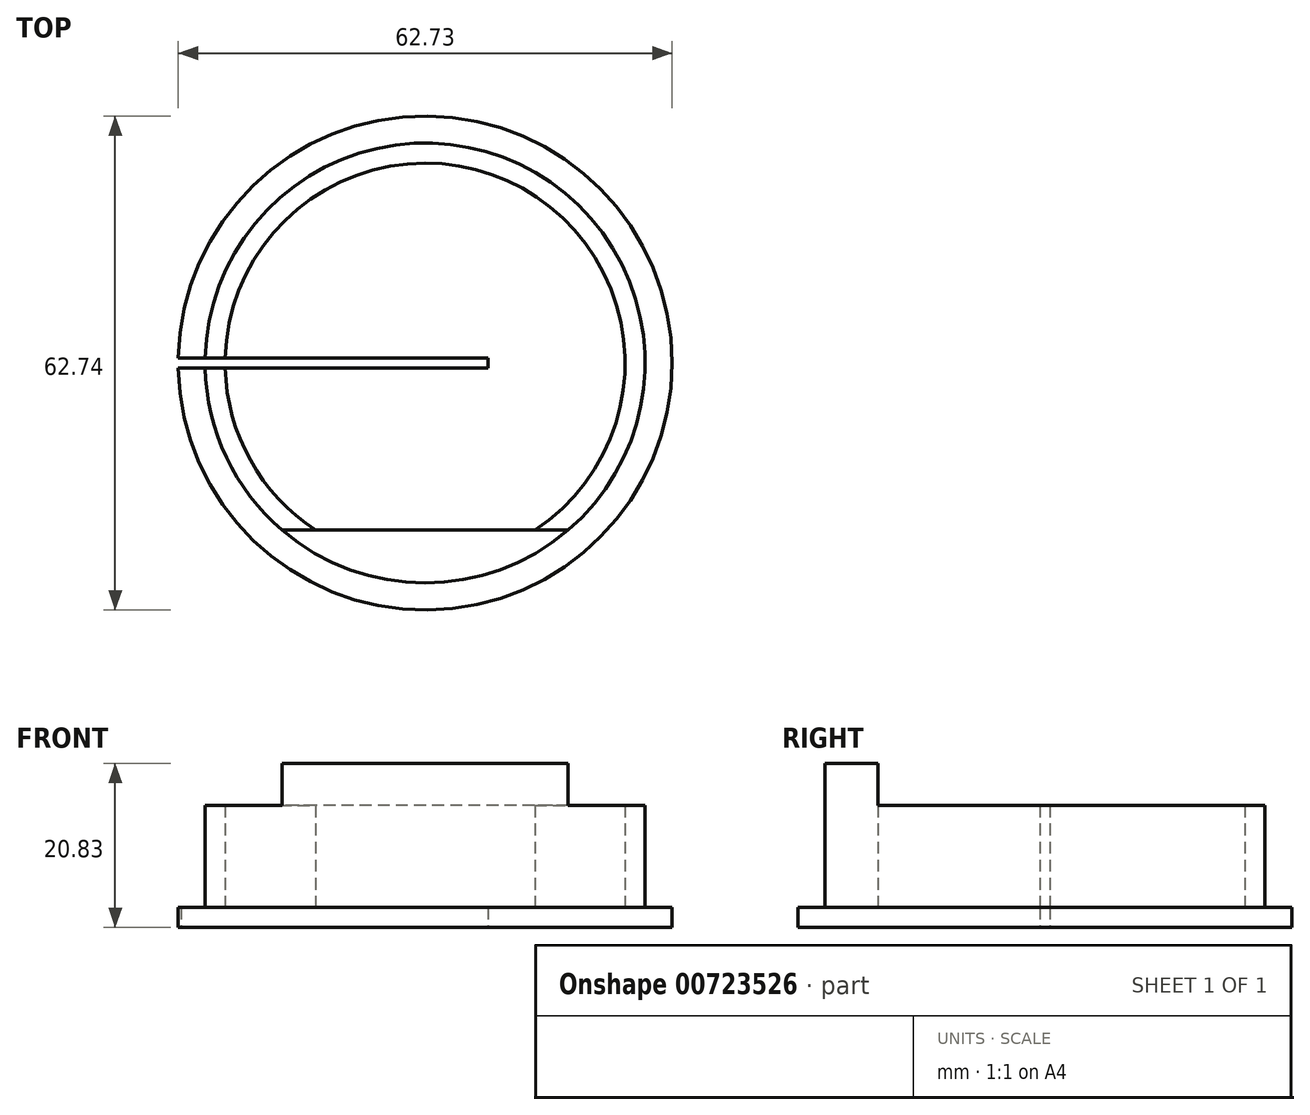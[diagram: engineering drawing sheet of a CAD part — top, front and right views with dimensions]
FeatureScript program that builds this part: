
annotation { "Feature Type Name" : "Feature", "Feature Type Description" : "" }
export const myFeature = defineFeature(function(context is Context, id is Id, definition is map)
    precondition{}
    {
        {
            var Q0;
            Q0=qCreatedBy(makeId("Top.planeOp"),FACE);
            var sketch = newSketch(context, id + "F0", { "sketchPlane" : qUnion([Q0])});
            skCircle(sketch, "E0", {"center": v(0, 0) * mm, "radius": 31.37 * mm});
            skSolve(sketch);
        }
        {
            var Q0;
            Q0=makeQuery(id+"F0.imprint","IMPRINT",FACE,{"disambiguationData":[TD([[makeQuery(id+"F0.imprint","IMPRINT",EDGE,{"derivedFrom":sQuery(id+"F0.wireOp",EDGE,"E0")}),1.0]])]});
            extrude(context, id + "F1", {"entities" : qUnion([Q0]), "depth" : 2.54 * mm, "offsetDistance" : 25.4 * mm});
        }
        {
            var Q0;
            Q0=qCreatedBy(makeId("Top.planeOp"),FACE);
            var sketch = newSketch(context, id + "F2", { "sketchPlane" : qUnion([Q0])});
            skCircle(sketch, "E1", {"center": v(0, 0) * mm, "radius": 27.94 * mm});
            skCircle(sketch, "E2", {"center": v(0, 0) * mm, "radius": 25.4 * mm});
            skSolve(sketch);
        }
        {
            var Q0;
            Q0=makeQuery(id+"F2.imprint","IMPRINT",FACE,{"disambiguationData":[TD([[makeQuery(id+"F2.imprint","IMPRINT",EDGE,{"derivedFrom":sQuery(id+"F2.wireOp",EDGE,"E1")}),1.0]])]});
            extrude(context, id + "F3", {"entities" : qUnion([Q0]), "operationType" : NewBodyOperationType.ADD, "depth" : 15.5 * mm, "offsetDistance" : 25.4 * mm});
        }
        {
            var Q0;
            Q0=makeQuery(id+"F0.imprint","IMPRINT",FACE,{"disambiguationData":[TD([[makeQuery(id+"F0.imprint","IMPRINT",EDGE,{"derivedFrom":sQuery(id+"F0.wireOp",EDGE,"E0")}),1.0]])]});
            var sketch = newSketch(context, id + "F4", { "sketchPlane" : qUnion([Q0])});
            skLineSegment(sketch, "E3", {"start": v(0, 0) * mm, "end": v(0, -0.63) * mm});
            skLineSegment(sketch, "E4", {"start": v(0, 0) * mm, "end": v(0, 0.63) * mm});
            skLineSegment(sketch, "E5", {"start": v(0, 0.64) * mm, "end": v(-31.33, 0.64) * mm});
            skLineSegment(sketch, "E6", {"start": v(0, -0.64) * mm, "end": v(-31.33, -0.64) * mm});
            skLineSegment(sketch, "E7", {"start": v(-31.33, 0.64) * mm, "end": v(-31.98, 0.64) * mm});
            skLineSegment(sketch, "E8", {"start": v(-31.98, 0.64) * mm, "end": v(-31.98, -0.65) * mm});
            skLineSegment(sketch, "E9", {"start": v(-31.98, -0.65) * mm, "end": v(-31.01, -0.64) * mm});
            skLineSegment(sketch, "E10", {"start": v(0, 0.64) * mm, "end": v(4.67, 0.64) * mm});
            skLineSegment(sketch, "E11", {"start": v(4.67, 0.64) * mm, "end": v(7.97, 0.64) * mm});
            skLineSegment(sketch, "E12", {"start": v(0, -0.64) * mm, "end": v(7.97, -0.64) * mm});
            skLineSegment(sketch, "E13", {"start": v(7.97, -0.64) * mm, "end": v(7.97, 0.64) * mm});
            skSolve(sketch);
        }
        {
            var Q0;
            {var subQ1=sQuery(id+"F4.wireOp",EDGE,"E3");Q0=makeQuery(id+"F4.imprint","IMPRINT",FACE,{"disambiguationData":[TD([[makeQuery(id+"F4.imprint","IMPRINT",EDGE,{"derivedFrom":subQ1}),-1.0]])]});}
            var Q1;
            {var subQ0=sQuery(id+"F4.wireOp",EDGE,"E8");Q1=makeQuery(id+"F4.imprint","IMPRINT",FACE,{"disambiguationData":[TD([[makeQuery(id+"F4.imprint","IMPRINT",EDGE,{"derivedFrom":subQ0}),1.0]])]});}
            var Q2;
            Q2=makeQuery(id+"F4.imprint","IMPRINT",FACE,{"disambiguationData":[TD([[makeQuery(id+"F4.imprint","IMPRINT",EDGE,{"derivedFrom":sQuery(id+"F4.wireOp",EDGE,"E3")}),1.0]])]});
            extrude(context, id + "F5", {"entities" : qUnion([Q0, Q1, Q2]), "operationType" : NewBodyOperationType.REMOVE, "depth" : 25.4 * mm, "offsetDistance" : 25.4 * mm});
        }
        {
            var Q0;
            Q0=qCreatedBy(makeId("Top.planeOp"),FACE);
            var sketch = newSketch(context, id + "F6", { "sketchPlane" : qUnion([Q0])});
            skCircle(sketch, "E14", {"center": v(0, 0) * mm, "radius": 27.94 * mm});
            skLineSegment(sketch, "E15", {"start": v(-18.16, -21.23) * mm, "end": v(18.16, -21.23) * mm});
            skSolve(sketch);
        }
        {
            var Q0;
            {var subQ0=sQuery(id+"F6.wireOp",EDGE,"E15");Q0=makeQuery(id+"F6.imprint","IMPRINT",FACE,{"disambiguationData":[TD([[makeQuery(id+"F6.imprint","IMPRINT",EDGE,{"derivedFrom":subQ0}),-1.0]])]});}
            extrude(context, id + "F7", {"entities" : qUnion([Q0]), "operationType" : NewBodyOperationType.ADD, "depth" : 20.83 * mm, "offsetDistance" : 25.4 * mm});
        }
    });
